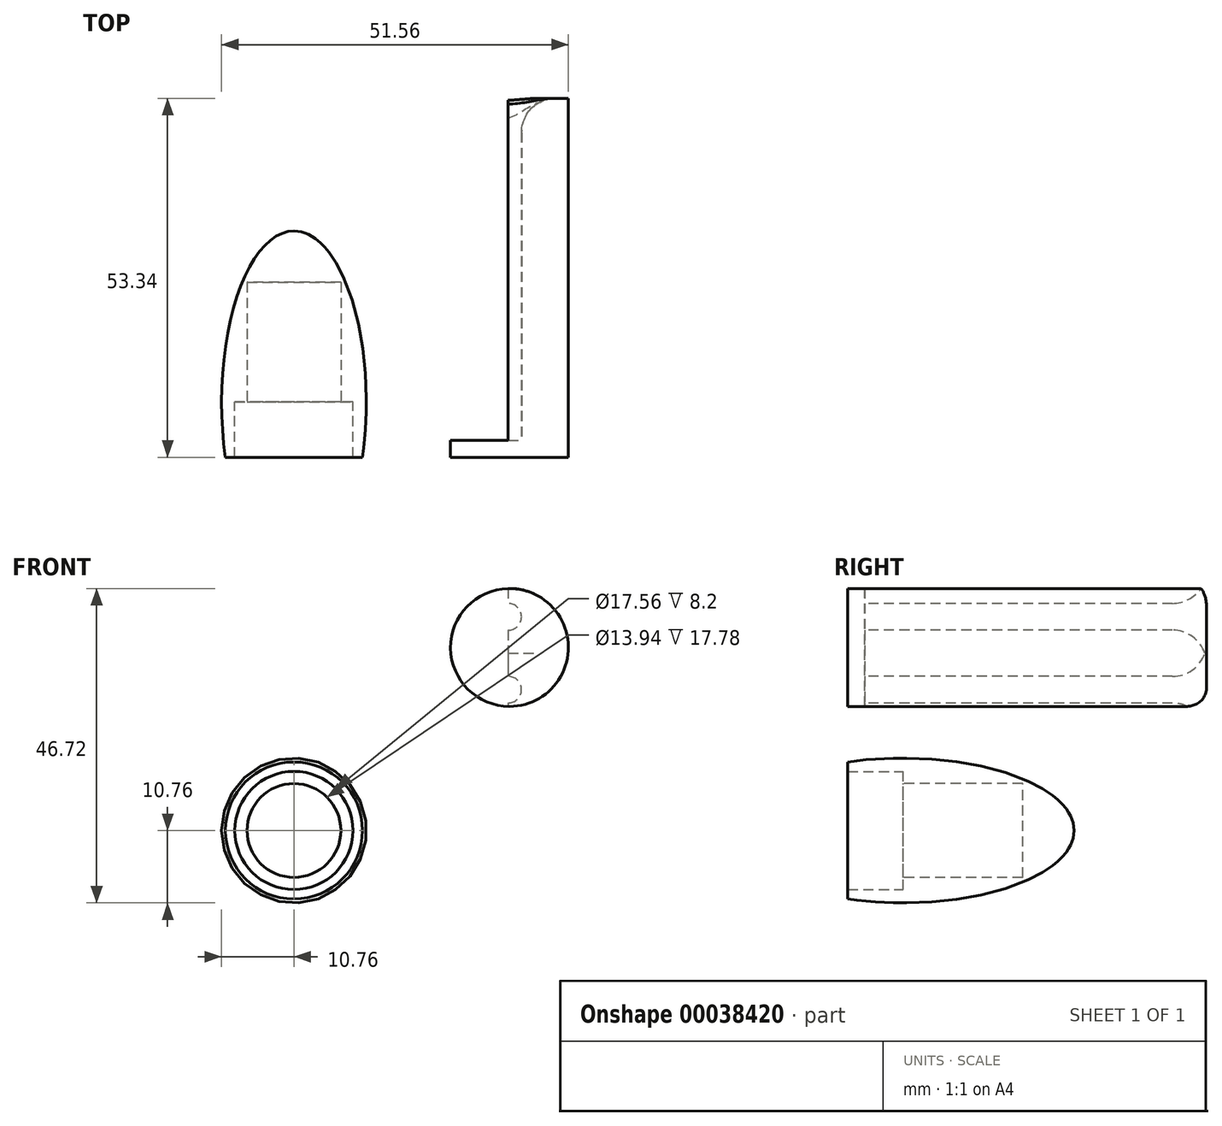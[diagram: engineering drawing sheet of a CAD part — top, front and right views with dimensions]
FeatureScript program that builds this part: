
annotation { "Feature Type Name" : "Feature", "Feature Type Description" : "" }
export const myFeature = defineFeature(function(context is Context, id is Id, definition is map)
    precondition{}
    {
        {
            var Q0;
            Q0=qCreatedBy(makeId("Top.planeOp"),FACE);
            var sketch = newSketch(context, id + "F0", { "sketchPlane" : qUnion([Q0])});
            skEllipse(sketch, "E0", {"center": v(0, 0) * mm, "majorRadius": 25.42 * mm, "minorRadius": 10.76 * mm, "majorAxis": v(0, 1)});
            skLineSegment(sketch, "E1", {"start": v(0, 25.42) * mm, "end": v(0, -25.42) * mm});
            skSolve(sketch);
        }
        {
            var Q0;
            {var subQ0=sQuery(id+"F0.wireOp",EDGE,"E1");Q0=makeQuery(id+"F0.imprint","IMPRINT",FACE,{"disambiguationData":[TD([[makeQuery(id+"F0.imprint","IMPRINT",EDGE,{"derivedFrom":subQ0}),-1.0]])]});}
            var Q1;
            Q1=sQuery(id+"F0.wireOp",EDGE,"E1");
            revolve(context, id + "F1", {"entities" : qUnion([Q0]), "axis" : qUnion([Q1]), "revolveType" : RevolveType.FULL});
        }
        {
            var Q0;
            Q0=qCreatedBy(makeId("Top.planeOp"),FACE);
            var sketch = newSketch(context, id + "F2", { "sketchPlane" : qUnion([Q0])});
            skLineSegment(sketch, "E2.bottom", {"start": v(-21.96, -29.97) * mm, "end": v(26.3, -29.97) * mm});
            skLineSegment(sketch, "E2.top", {"start": v(-21.96, -8.2) * mm, "end": v(26.3, -8.2) * mm});
            skLineSegment(sketch, "E2.left", {"start": v(-21.96, -29.97) * mm, "end": v(-21.96, -8.2) * mm});
            skLineSegment(sketch, "E2.right", {"start": v(26.3, -29.97) * mm, "end": v(26.3, -8.2) * mm});
            skLineSegment(sketch, "E3", {"start": v(0, 0) * mm, "end": v(0, -8.2) * mm});
            skSolve(sketch);
        }
        {
            var Q0;
            Q0 = qSketchRegion(id + "F2", true);
            var Q1;
            Q1=makeQuery(id+"F2.imprint","IMPRINT",FACE,{"disambiguationData":[TD([[makeQuery(id+"F2.imprint","IMPRINT",EDGE,{"derivedFrom":sQuery(id+"F2.wireOp",EDGE,"E2.bottom")}),1.0]])]});
            extrude(context, id + "F3", {"entities" : qUnion([Q0, Q1]), "operationType" : NewBodyOperationType.REMOVE, "endBound" : BoundingType.SYMMETRIC, "oppositeDirection" : true, "depth" : 101.6 * mm});
        }
        {
            var Q0;
            Q0=qCreatedBy(makeId("Front.planeOp"),FACE);
            var sketch = newSketch(context, id + "F4", { "sketchPlane" : qUnion([Q0])});
            skCircle(sketch, "E4", {"center": v(0, 0) * mm, "radius": 8.78 * mm});
            skLineSegment(sketch, "E5", {"start": v(0, 0) * mm, "end": v(6.48, 5.92) * mm});
            skSolve(sketch);
        }
        {
            var Q0;
            Q0 = qSketchRegion(id + "F4", true);
            extrude(context, id + "F5", {"entities" : qUnion([Q0]), "operationType" : NewBodyOperationType.REMOVE, "depth" : 25.4 * mm});
        }
        {
            var Q0;
            Q0=qCreatedBy(makeId("Front.planeOp"),FACE);
            var sketch = newSketch(context, id + "F6", { "sketchPlane" : qUnion([Q0])});
            skCircle(sketch, "E6", {"center": v(0, 0) * mm, "radius": 6.97 * mm});
            skSolve(sketch);
        }
        {
            var Q0;
            Q0 = qSketchRegion(id + "F6", true);
            extrude(context, id + "F7", {"entities" : qUnion([Q0]), "operationType" : NewBodyOperationType.REMOVE, "oppositeDirection" : true, "depth" : 17.78 * mm});
        }
        {
            var Q0;
            Q0=qCreatedBy(makeId("Front.planeOp"),FACE);
            var sketch = newSketch(context, id + "F8", { "sketchPlane" : qUnion([Q0])});
            skCircle(sketch, "E7", {"center": v(-32.04, 27.2) * mm, "radius": 8.76 * mm});
            skLineSegment(sketch, "E8", {"start": v(-32.04, 27.2) * mm, "end": v(-24.64, 31.88) * mm});
            skSolve(sketch);
        }
        {
            var Q0;
            Q0 = qSketchRegion(id + "F8", true);
            extrude(context, id + "F9", {"entities" : qUnion([Q0]), "depth" : 2.54 * mm});
        }
        {
            var Q0;
            Q0=makeQuery(id+"F9.opExtrude","CAP_FACE",FACE,{"disambiguationData":[OSD([sQuery(id+"F8.wireOp",EDGE,"E7")])],"isStart":false});
            var sketch = newSketch(context, id + "F10", { "sketchPlane" : qUnion([Q0])});
            skLineSegment(sketch, "E9", {"start": v(-31.84, 35.96) * mm, "end": v(-31.84, 0) * mm});
            skCircle(sketch, "E10", {"center": v(-31.84, 31.75) * mm, "radius": 1.99 * mm});
            skLineSegment(sketch, "E11", {"start": v(-31.84, 31.75) * mm, "end": v(-29.86, 31.75) * mm});
            skCircle(sketch, "E12", {"center": v(-31.84, 20.93) * mm, "radius": 1.98 * mm});
            skLineSegment(sketch, "E13", {"start": v(-29.87, 21.1) * mm, "end": v(-31.84, 20.93) * mm});
            skSolve(sketch);
        }
        {
            var Q0;
            {var subQ1=sQuery(id+"F10.wireOp",EDGE,"E9");var subQ4=makeQuery(id+"F10.imprint","INTERSECT",VERTEX,{"derivedFrom":[subQ1,sQuery(id+"F10.wireOp",EDGE,"E11")]});Q0=makeQuery(id+"F10.imprint","IMPRINT",FACE,{"disambiguationData":[TD([[makeQuery(id+"F10.imprint","IMPRINT",EDGE,{"disambiguationData":[TD([[subQ4,1.0]])],"derivedFrom":subQ1}),-1.0]])]});}
            var Q1;
            {var subQ0=sQuery(id+"F10.wireOp",EDGE,"E11");Q1=makeQuery(id+"F10.imprint","IMPRINT",FACE,{"disambiguationData":[TD([[makeQuery(id+"F10.imprint","IMPRINT",EDGE,{"derivedFrom":subQ0}),1.0]])]});}
            var Q2;
            {var subQ0=sQuery(id+"F10.wireOp",EDGE,"E11");Q2=makeQuery(id+"F10.imprint","IMPRINT",FACE,{"disambiguationData":[TD([[makeQuery(id+"F10.imprint","IMPRINT",EDGE,{"derivedFrom":subQ0}),-1.0]])]});}
            var Q3;
            {var subQ1=sQuery(id+"F10.wireOp",EDGE,"E9");var subQ4=makeQuery(id+"F10.imprint","INTERSECT",VERTEX,{"derivedFrom":[subQ1,sQuery(id+"F10.wireOp",EDGE,"E13")]});Q3=makeQuery(id+"F10.imprint","IMPRINT",FACE,{"disambiguationData":[TD([[makeQuery(id+"F10.imprint","IMPRINT",EDGE,{"disambiguationData":[TD([[subQ4,1.0]])],"derivedFrom":subQ1}),-1.0]])]});}
            var Q4;
            {var subQ0=sQuery(id+"F10.wireOp",EDGE,"E13");Q4=makeQuery(id+"F10.imprint","IMPRINT",FACE,{"disambiguationData":[TD([[makeQuery(id+"F10.imprint","IMPRINT",EDGE,{"derivedFrom":subQ0}),-1.0]])]});}
            var Q5;
            {var subQ0=sQuery(id+"F10.wireOp",EDGE,"E13");Q5=makeQuery(id+"F10.imprint","IMPRINT",FACE,{"disambiguationData":[TD([[makeQuery(id+"F10.imprint","IMPRINT",EDGE,{"derivedFrom":subQ0}),1.0]])]});}
            extrude(context, id + "F11", {"entities" : qUnion([Q0, Q1, Q2, Q3, Q4, Q5]), "operationType" : NewBodyOperationType.ADD, "depth" : 50.8 * mm});
        }
        {
            var Q0;
            Q0=qCreatedBy(makeId("Right.planeOp"),FACE);
            var sketch = newSketch(context, id + "F12", { "sketchPlane" : qUnion([Q0])});
            skLineSegment(sketch, "E14", {"start": v(0, 54.5) * mm, "end": v(0, 0) * mm});
            skSolve(sketch);
        }
        {
            var Q0;
            Q0=makeQuery(id+"F9.opExtrude","SWEPT_BODY",BODY,{"disambiguationData":[OSD([sQuery(id+"F8.wireOp",EDGE,"E7")])]});
            var Q1;
            Q1=sQuery(id+"F12.wireOp",EDGE,"E14");
            transform(context, id + "F13", {"entities" : qUnion([Q0]), "transformType" : TransformType.ROTATION, "transformAxis" : qUnion([Q1]), "angle" : 180 * degree, "makeCopy" : false});
        }
        {
            var Q0;
            Q0=makeQuery(id+"F1.opRevolve","SWEPT_BODY",BODY,{"disambiguationData":[OSD([sQuery(id+"F0.wireOp",EDGE,"E0"),sQuery(id+"F0.wireOp",EDGE,"E1")])]});
            transform(context, id + "F14", {"entities" : qUnion([Q0]), "transformType" : TransformType.TRANSLATION_3D, "dx" : 0 * mm, "dy" : 8.2 * mm, "dz" : 0 * mm, "makeCopy" : false});
        }
        {
            var Q0;
            Q0=makeQuery(id+"F11.opExtrude","CAP_EDGE",EDGE,{"disambiguationData":[OSD([sQuery(id+"F10.wireOp",EDGE,"E10")])],"isStart":false});
            var Q1;
            Q1=makeQuery(id+"F11.opExtrude","CAP_EDGE",EDGE,{"disambiguationData":[OSD([sQuery(id+"F10.wireOp",EDGE,"E12")])],"isStart":false});
            fillet(context, id + "F15", {"entities" : qUnion([Q0, Q1]), "radius" : 5.08 * mm, "tangentPropagation" : true, "allowEdgeOverflow" : false});
        }
    });
